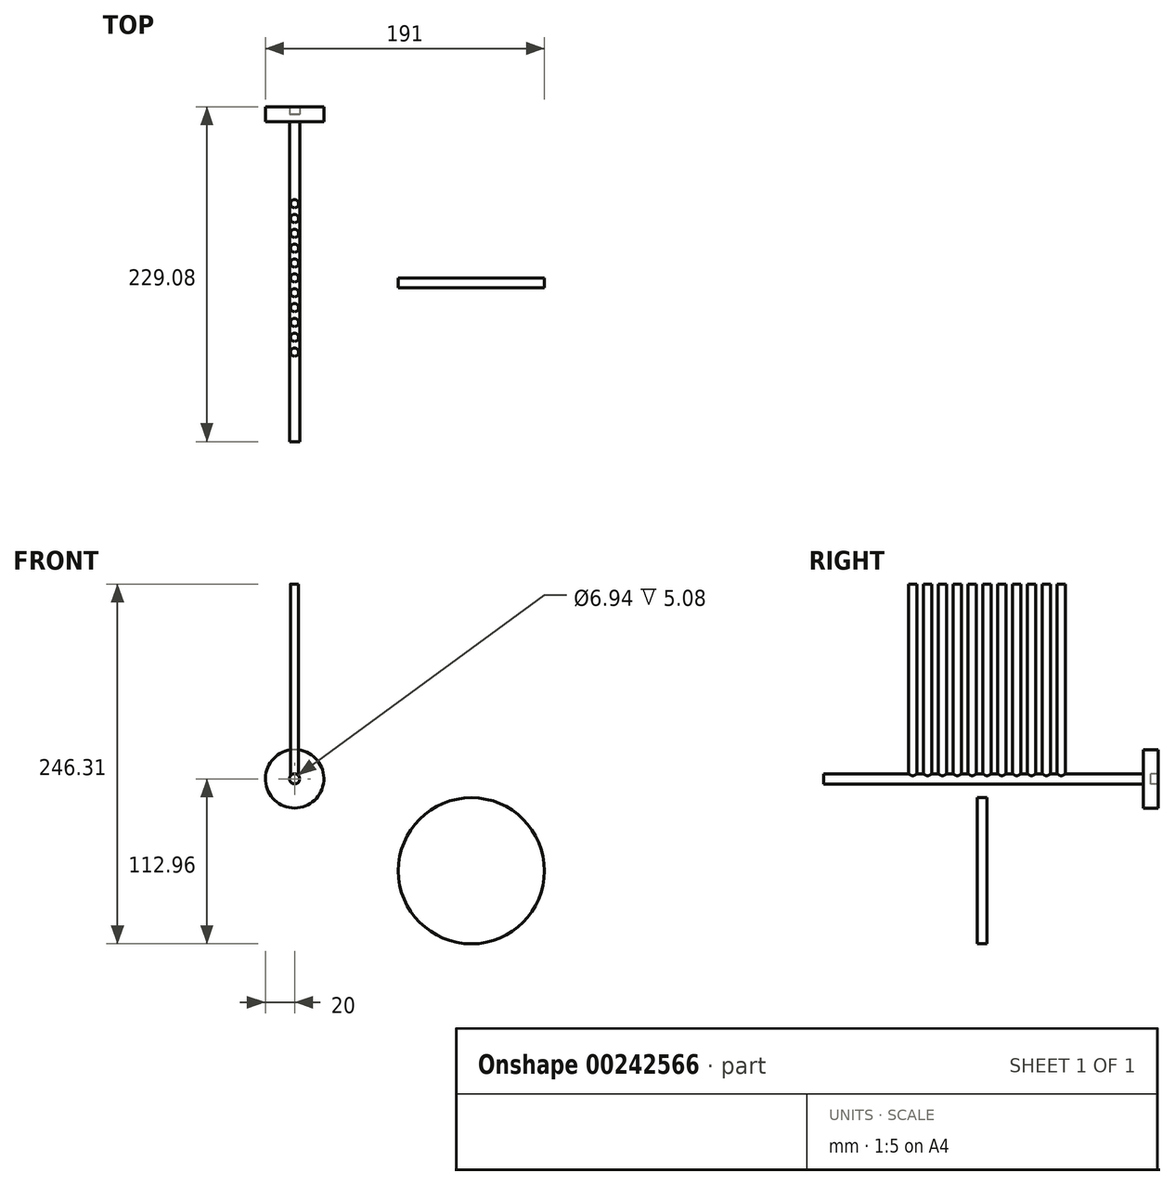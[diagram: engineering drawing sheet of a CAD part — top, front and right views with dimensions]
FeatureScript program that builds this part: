
annotation { "Feature Type Name" : "Feature", "Feature Type Description" : "" }
export const myFeature = defineFeature(function(context is Context, id is Id, definition is map)
    precondition{}
    {
        {
            var Q0;
            Q0=qCreatedBy(makeId("Front.planeOp"),FACE);
            var sketch = newSketch(context, id + "F0", { "sketchPlane" : qUnion([Q0])});
            skCircle(sketch, "E0", {"center": v(0, 0) * mm, "radius": 3.47 * mm});
            skSolve(sketch);
        }
        {
            var Q0;
            Q0 = qSketchRegion(id + "F0", true);
            extrude(context, id + "F1", {"entities" : qUnion([Q0]), "endBound" : BoundingType.SYMMETRIC, "depth" : 7 * 32 * mm});
        }
        {
            var Q0;
            Q0=qCreatedBy(makeId("Top.planeOp"),FACE);
            var sketch = newSketch(context, id + "F2", { "sketchPlane" : qUnion([Q0])});
            skCircle(sketch, "E1", {"center": v(0, 0) * mm, "radius": 2.79 * mm});
            skCircle(sketch, "E2.0.1.0", {"center": v(0, 10.16) * mm, "radius": 2.79 * mm});
            skCircle(sketch, "E2.0.2.0", {"center": v(0, 20.32) * mm, "radius": 2.79 * mm});
            skCircle(sketch, "E2.0.3.0", {"center": v(0, 30.48) * mm, "radius": 2.79 * mm});
            skCircle(sketch, "E2.0.4.0", {"center": v(0, 40.64) * mm, "radius": 2.79 * mm});
            skCircle(sketch, "E2.0.5.0", {"center": v(0, 50.8) * mm, "radius": 2.79 * mm});
            skLineSegment(sketch, "E2.direction1", {"start": v(0, 0) * mm, "end": v(25.4, 0) * mm, "construction": true});
            skLineSegment(sketch, "E2.direction2", {"start": v(0, 0) * mm, "end": v(0, 10.16) * mm, "construction": true});
            skCircle(sketch, "E3.MirrorC", {"center": v(0, -10.16) * mm, "radius": 2.79 * mm});
            skCircle(sketch, "E4.MirrorC", {"center": v(0, -20.32) * mm, "radius": 2.79 * mm});
            skCircle(sketch, "E5.MirrorC", {"center": v(0, -30.48) * mm, "radius": 2.79 * mm});
            skCircle(sketch, "E6.MirrorC", {"center": v(0, -40.64) * mm, "radius": 2.79 * mm});
            skCircle(sketch, "E7.MirrorC", {"center": v(0, -50.8) * mm, "radius": 2.79 * mm});
            skSolve(sketch);
        }
        {
            var Q0;
            Q0 = qSketchRegion(id + "F2", true);
            extrude(context, id + "F3", {"entities" : qUnion([Q0]), "operationType" : NewBodyOperationType.ADD, "depth" : 133.35 * mm});
        }
        {
            var Q0;
            Q0=makeQuery(id+"F1.opExtrude","CAP_FACE",FACE,{"disambiguationData":[OSD([sQuery(id+"F0.wireOp",EDGE,"E0")])],"isStart":true});
            var sketch = newSketch(context, id + "F4", { "sketchPlane" : qUnion([Q0])});
            skCircle(sketch, "E8", {"center": v(0, 0) * mm, "radius": 20 * mm});
            skSolve(sketch);
        }
        {
            var Q0;
            Q0=makeQuery(id+"F4.imprint","IMPRINT",FACE,{"disambiguationData":[TD([[makeQuery(id+"F4.imprint","IMPRINT",EDGE,{"derivedFrom":sQuery(id+"F4.wireOp",EDGE,"E8")}),1.0]])]});
            extrude(context, id + "F5", {"entities" : qUnion([Q0]), "operationType" : NewBodyOperationType.ADD, "endBound" : BoundingType.SYMMETRIC, "depth" : 10.16 * mm});
        }
        {
            var Q0;
            Q0=qCreatedBy(makeId("Front.planeOp"),FACE);
            var sketch = newSketch(context, id + "F6", { "sketchPlane" : qUnion([Q0])});
            skCircle(sketch, "E9", {"center": v(121, -62.96) * mm, "radius": 50 * mm});
            skSolve(sketch);
        }
        {
            var Q0;
            Q0 = qSketchRegion(id + "F6", true);
            extrude(context, id + "F7", {"entities" : qUnion([Q0]), "depth" : 6.86 * mm});
        }
    });
